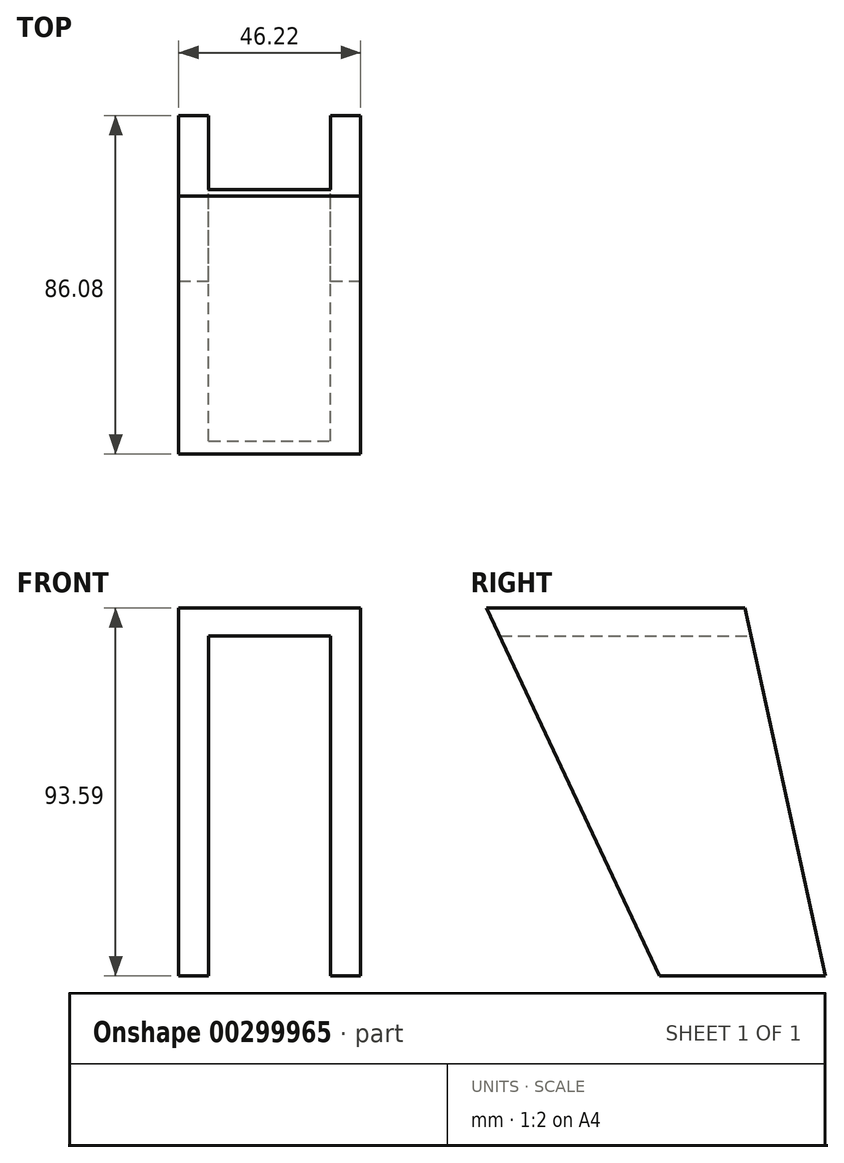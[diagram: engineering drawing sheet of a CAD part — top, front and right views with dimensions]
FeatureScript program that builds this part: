
annotation { "Feature Type Name" : "Feature", "Feature Type Description" : "" }
export const myFeature = defineFeature(function(context is Context, id is Id, definition is map)
    precondition{}
    {
        {
            var Q0;
            Q0=qCreatedBy(makeId("Right.planeOp"),FACE);
            var sketch = newSketch(context, id + "F0", { "sketchPlane" : qUnion([Q0])});
            skLineSegment(sketch, "E0", {"start": v(-47.3, 56.31) * mm, "end": v(18.33, 56.31) * mm});
            skLineSegment(sketch, "E1", {"start": v(38.79, -37.28) * mm, "end": v(18.33, 56.31) * mm});
            skLineSegment(sketch, "E2", {"start": v(38.79, -37.28) * mm, "end": v(-3.43, -37.28) * mm});
            skLineSegment(sketch, "E3", {"start": v(-3.43, -37.28) * mm, "end": v(-47.3, 56.31) * mm});
            skSolve(sketch);
        }
        {
            var Q0;
            Q0 = qSketchRegion(id + "F0", true);
            extrude(context, id + "F1", {"entities" : qUnion([Q0]), "endBound" : BoundingType.SYMMETRIC, "depth" : 46.23 * mm, "offsetDistance" : 25.4 * mm});
        }
        {
            var Q0;
            Q0=makeQuery(id+"F1.opExtrude","SWEPT_FACE",FACE,{"disambiguationData":[OSD([sQuery(id+"F0.wireOp",EDGE,"E2")])]});
            var sketch = newSketch(context, id + "F2", { "sketchPlane" : qUnion([Q0])});
            skLineSegment(sketch, "E4.bottom", {"start": v(-15.5, 51) * mm, "end": v(15.5, 51) * mm});
            skLineSegment(sketch, "E4.top", {"start": v(-15.5, -43.28) * mm, "end": v(15.5, -43.28) * mm});
            skLineSegment(sketch, "E4.left", {"start": v(-15.5, 51) * mm, "end": v(-15.5, -43.28) * mm});
            skLineSegment(sketch, "E4.right", {"start": v(15.5, 51) * mm, "end": v(15.5, -43.28) * mm});
            skSolve(sketch);
        }
        {
            var Q0;
            Q0 = qSketchRegion(id + "F2", true);
            extrude(context, id + "F3", {"entities" : qUnion([Q0]), "operationType" : NewBodyOperationType.REMOVE, "oppositeDirection" : true, "depth" : 86.36 * mm, "offsetDistance" : 25.4 * mm});
        }
    });
